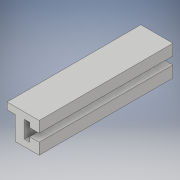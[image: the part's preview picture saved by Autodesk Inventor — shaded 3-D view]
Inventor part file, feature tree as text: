
AUTODESK INVENTOR PART (.ipt)
format: ipt  version: 2019 (Build 230136000, 136)  size: 112,128 bytes
history: native  units: mm
features: extrude x1, sketch x1
ambient origin geometry x8: Origin, YZ Plane, XZ Plane, XY Plane, X Axis, Y Axis, Z Axis, Center Point
bodies: Solid1 (feature_tree)
feature tree (2):
  extrude  "Extrusion1"  Depth=5.0mm
  sketch  "Sketch1"  dims[d0=6.0mm d1=5.0mm d4=4.0mm d8=5.0mm d10=5.8mm d12=3.5mm d13=3.5mm d15=100.0mm d16=0.0mm d17=0.3mm d18=18.0mm d19=7.0mm d20=0.0mm]
